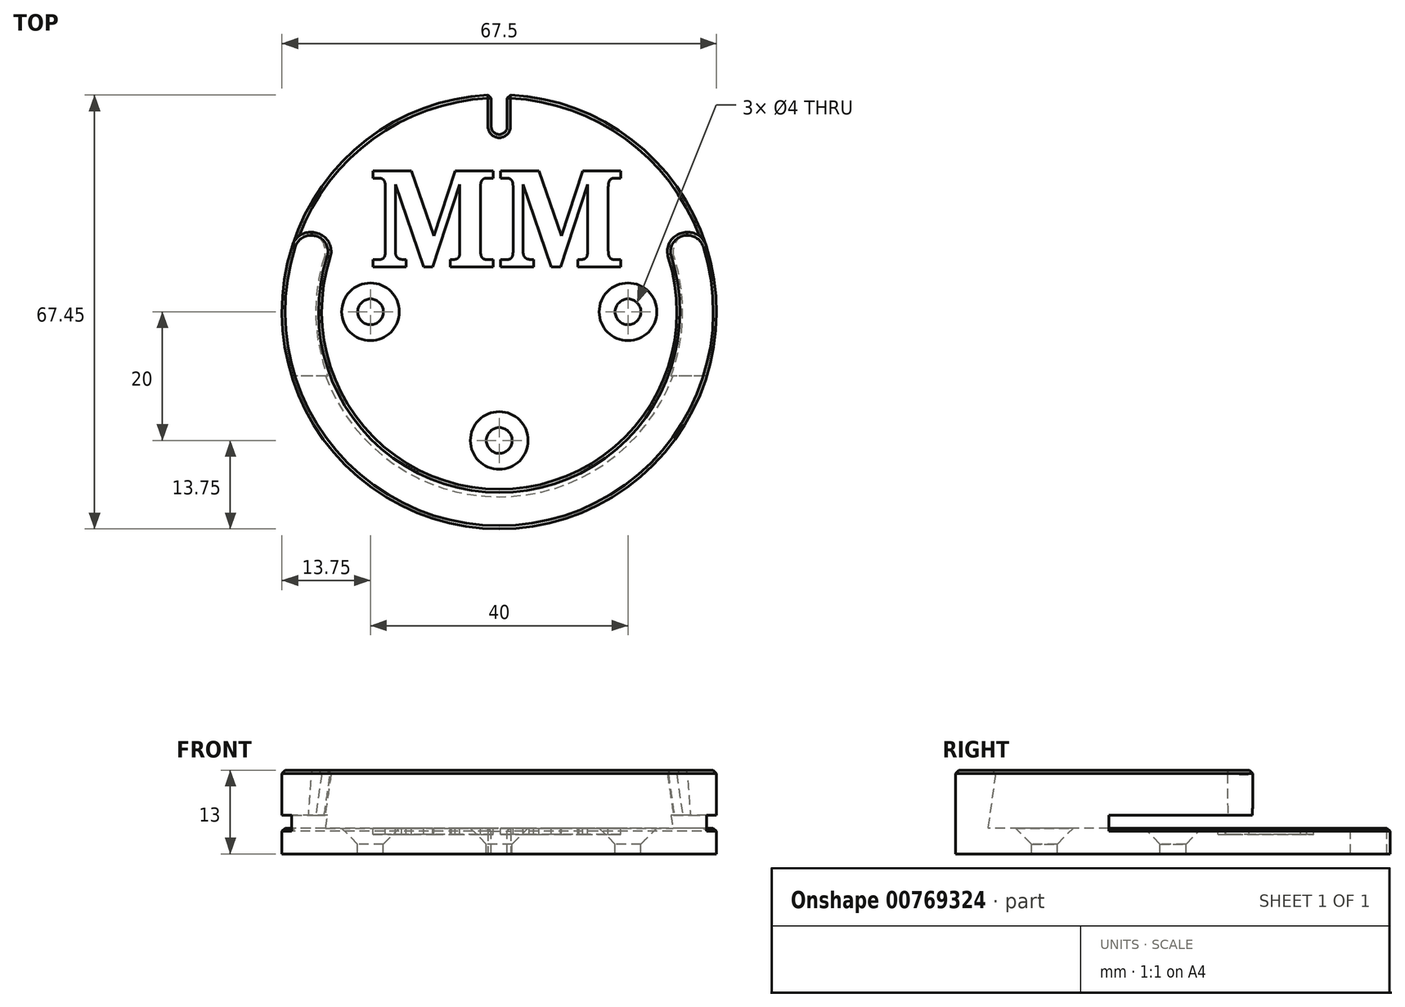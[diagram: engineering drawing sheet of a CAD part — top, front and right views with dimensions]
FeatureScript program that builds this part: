
annotation { "Feature Type Name" : "Feature", "Feature Type Description" : "" }
export const myFeature = defineFeature(function(context is Context, id is Id, definition is map)
    precondition{}
    {
        {
            var Q0;
            Q0=qCreatedBy(makeId("Top.planeOp"),FACE);
            var sketch = newSketch(context, id + "F0", { "sketchPlane" : qUnion([Q0])});
            skCircle(sketch, "E0", {"center": v(0, 0) * mm, "radius": 33.75 * mm});
            skSolve(sketch);
        }
        {
            var Q0;
            Q0 = qSketchRegion(id + "F0", true);
            extrude(context, id + "F1", {"entities" : qUnion([Q0]), "depth" : 13 * mm, "offsetDistance" : 25 * mm});
        }
        {
            var Q0;
            Q0=makeQuery(id+"F1.opExtrude","CAP_FACE",FACE,{"disambiguationData":[OSD([sQuery(id+"F0.wireOp",EDGE,"E0")])],"isStart":false});
            var sketch = newSketch(context, id + "F2", { "sketchPlane" : qUnion([Q0])});
            skCircle(sketch, "E1", {"center": v(0, 0) * mm, "radius": 27.5 * mm});
            skSolve(sketch);
        }
        {
            var Q0;
            Q0 = qSketchRegion(id + "F2", true);
            extrude(context, id + "F3", {"entities" : qUnion([Q0]), "operationType" : NewBodyOperationType.REMOVE, "oppositeDirection" : true, "depth" : 9 * mm, "offsetDistance" : 25 * mm, "hasDraft" : true, "draftAngle" : 8 * degree});
        }
        {
            var Q0;
            Q0=makeQuery(id+"F1.opExtrude","CAP_FACE",FACE,{"disambiguationData":[OSD([sQuery(id+"F0.wireOp",EDGE,"E0")])],"isStart":false});
            var sketch = newSketch(context, id + "F4", { "sketchPlane" : qUnion([Q0])});
            skLineSegment(sketch, "E2.bottom", {"start": v(-40, 56.82) * mm, "end": v(40, 56.82) * mm});
            skLineSegment(sketch, "E2.left", {"start": v(-40, 56.82) * mm, "end": v(-40, 12.37) * mm});
            skLineSegment(sketch, "E3", {"start": v(-40, 12.37) * mm, "end": v(40, 12.37) * mm});
            skLineSegment(sketch, "E4", {"start": v(40, 56.82) * mm, "end": v(40, 12.37) * mm});
            skSolve(sketch);
        }
        {
            var Q0;
            Q0 = qSketchRegion(id + "F4", true);
            extrude(context, id + "F5", {"entities" : qUnion([Q0]), "operationType" : NewBodyOperationType.REMOVE, "oppositeDirection" : true, "depth" : 9 * mm, "offsetDistance" : 25 * mm});
        }
        {
            var Q0;
            Q0=qCreatedBy(makeId("Front.planeOp"),FACE);
            var sketch = newSketch(context, id + "F6", { "sketchPlane" : qUnion([Q0])});
            skLineSegment(sketch, "E5.bottom", {"start": v(57, 6) * mm, "end": v(-73, 6) * mm});
            skLineSegment(sketch, "E5.top", {"start": v(57, 4) * mm, "end": v(-73, 4) * mm});
            skLineSegment(sketch, "E5.left", {"start": v(57, 6) * mm, "end": v(57, 4) * mm});
            skLineSegment(sketch, "E5.right", {"start": v(-73, 6) * mm, "end": v(-73, 4) * mm});
            skSolve(sketch);
        }
        {
            var Q0;
            Q0 = qSketchRegion(id + "F6", true);
            extrude(context, id + "F7", {"entities" : qUnion([Q0]), "operationType" : NewBodyOperationType.REMOVE, "depth" : 10 * mm, "offsetDistance" : 25 * mm, "hasSecondDirection" : true, "secondDirectionOppositeDirection" : true, "secondDirectionDepth" : 48.7 * mm});
        }
        {
            var Q0;
            Q0=makeQuery(id+"F7.boolean.opBoolean","MERGE",FACE,{"derivedFrom":[makeQuery(id+"F5.boolean.opBoolean","MERGE",FACE,{"derivedFrom":[makeQuery(id+"F3.boolean.opBoolean","COPY",FACE,{"derivedFrom":makeQuery(id+"F3.opExtrude","CAP_FACE",FACE,{"disambiguationData":[OSD([sQuery(id+"F2.wireOp",EDGE,"E1")])],"isStart":false})}),makeQuery(id+"F5.opExtrude","CAP_FACE",FACE,{"disambiguationData":[OSD([sQuery(id+"F4.wireOp",EDGE,"E2.bottom"),sQuery(id+"F4.wireOp",EDGE,"E2.top"),sQuery(id+"F4.wireOp",EDGE,"E2.left"),sQuery(id+"F4.wireOp",EDGE,"E2.right")])],"isStart":false})]}),makeQuery(id+"F7.opExtrude","SWEPT_FACE",FACE,{"disambiguationData":[OSD([sQuery(id+"F6.wireOp",EDGE,"E5.top")])]})]});
            var sketch = newSketch(context, id + "F8", { "sketchPlane" : qUnion([Q0])});
            skText(sketch, "E6", { "text": "MM", "fontName": "NotoSerif-Bold.ttf"});
            const initialGuessF8  = {"E6": [-0.02022, 0.007, 1, 0, 0.015]};
            skSetInitialGuess(sketch, initialGuessF8);
            skSolve(sketch);
        }
        {
            var Q0;
            Q0 = qSketchRegion(id + "F8", true);
            extrude(context, id + "F9", {"entities" : qUnion([Q0]), "operationType" : NewBodyOperationType.REMOVE, "oppositeDirection" : true, "depth" : 1 * mm, "offsetDistance" : 25 * mm});
        }
        {
            var Q0;
            Q0=makeQuery(id+"F5.boolean.opBoolean","INTERSECT",EDGE,{"disambiguationData":[OD(0.0)],"derivedFrom":[makeQuery(id+"F3.boolean.opBoolean","COPY",FACE,{"derivedFrom":makeQuery(id+"F3.opExtrude","SWEPT_FACE",FACE,{"disambiguationData":[OSD([sQuery(id+"F2.wireOp",EDGE,"E1")])]})}),makeQuery(id+"F5.opExtrude","SWEPT_FACE",FACE,{"disambiguationData":[OSD([sQuery(id+"F4.wireOp",EDGE,"E3")])]})]});
            var Q1;
            Q1=makeQuery(id+"F5.boolean.opBoolean","INTERSECT",EDGE,{"disambiguationData":[OD(0.0)],"derivedFrom":[makeQuery(id+"F1.opExtrude","SWEPT_FACE",FACE,{"disambiguationData":[OSD([sQuery(id+"F0.wireOp",EDGE,"E0")])]}),makeQuery(id+"F5.opExtrude","SWEPT_FACE",FACE,{"disambiguationData":[OSD([sQuery(id+"F4.wireOp",EDGE,"E3")])]})]});
            var Q2;
            Q2=makeQuery(id+"F5.boolean.opBoolean","INTERSECT",EDGE,{"disambiguationData":[OD(1.0)],"derivedFrom":[makeQuery(id+"F1.opExtrude","SWEPT_FACE",FACE,{"disambiguationData":[OSD([sQuery(id+"F0.wireOp",EDGE,"E0")])]}),makeQuery(id+"F5.opExtrude","SWEPT_FACE",FACE,{"disambiguationData":[OSD([sQuery(id+"F4.wireOp",EDGE,"E3")])]})]});
            var Q3;
            Q3=makeQuery(id+"F5.boolean.opBoolean","INTERSECT",EDGE,{"disambiguationData":[OD(1.0)],"derivedFrom":[makeQuery(id+"F3.boolean.opBoolean","COPY",FACE,{"derivedFrom":makeQuery(id+"F3.opExtrude","SWEPT_FACE",FACE,{"disambiguationData":[OSD([sQuery(id+"F2.wireOp",EDGE,"E1")])]})}),makeQuery(id+"F5.opExtrude","SWEPT_FACE",FACE,{"disambiguationData":[OSD([sQuery(id+"F4.wireOp",EDGE,"E3")])]})]});
            fillet(context, id + "F10", {"entities" : qUnion([Q0, Q1, Q2, Q3]), "radius" : 3 * mm, "tangentPropagation" : true, "allowEdgeOverflow" : false});
        }
        {
            var Q0;
            Q0=makeQuery(id+"F1.opExtrude","CAP_EDGE",EDGE,{"disambiguationData":[OSD([sQuery(id+"F0.wireOp",EDGE,"E0")])],"isStart":false});
            chamfer(context, id + "F11", {"entities" : qUnion([Q0]), "width" : 0.5 * mm, "tangentPropagation" : true});
        }
        {
            var Q0;
            Q0=makeQuery(id+"F7.boolean.opBoolean","MERGE",FACE,{"derivedFrom":[makeQuery(id+"F5.boolean.opBoolean","MERGE",FACE,{"derivedFrom":[makeQuery(id+"F3.boolean.opBoolean","COPY",FACE,{"derivedFrom":makeQuery(id+"F3.opExtrude","CAP_FACE",FACE,{"disambiguationData":[OSD([sQuery(id+"F2.wireOp",EDGE,"E1")])],"isStart":false})}),makeQuery(id+"F5.opExtrude","CAP_FACE",FACE,{"disambiguationData":[OSD([sQuery(id+"F4.wireOp",EDGE,"E2.bottom"),sQuery(id+"F4.wireOp",EDGE,"E2.left"),sQuery(id+"F4.wireOp",EDGE,"E3"),sQuery(id+"F4.wireOp",EDGE,"E4")])],"isStart":false})]}),makeQuery(id+"F7.opExtrude","SWEPT_FACE",FACE,{"disambiguationData":[OSD([sQuery(id+"F6.wireOp",EDGE,"E5.top")])]})]});
            var sketch = newSketch(context, id + "F12", { "sketchPlane" : qUnion([Q0])});
            skPoint(sketch, "E7", {"position": v(20, 0) * mm});
            skPoint(sketch, "E8", {"position": v(0, -20) * mm});
            skPoint(sketch, "E9", {"position": v(-20, 0) * mm});
            skSolve(sketch);
        }
        {
            var Q0;
            Q0=sQuery(id+"F12.wireOp",VERTEX,"E8");
            var Q1;
            Q1=sQuery(id+"F12.wireOp",VERTEX,"E7");
            var Q2;
            Q2=sQuery(id+"F12.wireOp",VERTEX,"E9");
            var Q3;
            Q3=makeQuery(id+"F1.opExtrude","SWEPT_BODY",BODY,{"disambiguationData":[OSD([sQuery(id+"F0.wireOp",EDGE,"E0")])]});
            hole(context, id + "F13", {"style" : HoleStyle.C_SINK, "endStyle" : HoleEndStyle.THROUGH, "holeDiameter" : 4 * mm, "cSinkDiameter" : 8.96 * mm, "cSinkAngle" : 90 * degree, "majorDiameter" : 5 * mm, "isTappedThrough" : true, "tappedDepth" : 12 * mm, "tapClearance" : 3, "startFromSketch" : true, "locations" : qUnion([Q0, Q1, Q2]), "scope" : qUnion([Q3])});
        }
        {
            var Q0;
            Q0=makeQuery(id+"F2.imprint","IMPRINT",FACE,{"disambiguationData":[TD([[makeQuery(id+"F2.imprint","IMPRINT",EDGE,{"derivedFrom":sQuery(id+"F2.wireOp",EDGE,"E1")}),-1.0]])]});
            var sketch = newSketch(context, id + "F14", { "sketchPlane" : qUnion([Q0])});
            skLineSegment(sketch, "E10.bottom", {"start": v(-1.25, 36.81) * mm, "end": v(1.25, 36.81) * mm});
            skLineSegment(sketch, "E10.left", {"start": v(-1.25, 36.81) * mm, "end": v(-1.25, 28.81) * mm});
            skLineSegment(sketch, "E10.right", {"start": v(1.25, 36.81) * mm, "end": v(1.25, 28.81) * mm});
            skArc(sketch, "E11", {"start": v(-1.25, 28.81) * mm, "mid": v(0, 27.56) * mm, "end": v(1.25, 28.81) * mm});
            skSolve(sketch);
        }
        {
            var Q0;
            Q0 = qSketchRegion(id + "F14", true);
            extrude(context, id + "F15", {"entities" : qUnion([Q0]), "operationType" : NewBodyOperationType.REMOVE, "oppositeDirection" : true, "depth" : 25 * mm, "offsetDistance" : 25 * mm});
        }
        {
            var Q0;
            {var subQ0=sQuery(id+"F6.wireOp",EDGE,"E5.top");var subQ1=makeQuery(id+"F7.opExtrude","SWEPT_FACE",FACE,{"disambiguationData":[OSD([subQ0])]});var subQ2=makeQuery(id+"F1.opExtrude","SWEPT_FACE",FACE,{"disambiguationData":[OSD([sQuery(id+"F0.wireOp",EDGE,"E0")])]});Q0=makeQuery(id+"F15.boolean.opBoolean","SPLIT",EDGE,{"disambiguationData":[TD([makeQuery(id+"F15.opExtrude","SWEPT_FACE",FACE,{"disambiguationData":[OSD([sQuery(id+"F14.wireOp",EDGE,"E10.right")])]})])],"derivedFrom":makeQuery(id+"F7.boolean.opBoolean","INTERSECT",EDGE,{"derivedFrom":[subQ2,subQ1]})});}
            var Q1;
            {var subQ0=sQuery(id+"F6.wireOp",EDGE,"E5.top");var subQ1=makeQuery(id+"F7.opExtrude","SWEPT_FACE",FACE,{"disambiguationData":[OSD([subQ0])]});var subQ2=makeQuery(id+"F1.opExtrude","SWEPT_FACE",FACE,{"disambiguationData":[OSD([sQuery(id+"F0.wireOp",EDGE,"E0")])]});Q1=makeQuery(id+"F15.boolean.opBoolean","SPLIT",EDGE,{"disambiguationData":[TD([makeQuery(id+"F15.opExtrude","SWEPT_FACE",FACE,{"disambiguationData":[OSD([sQuery(id+"F14.wireOp",EDGE,"E10.left")])]})])],"derivedFrom":makeQuery(id+"F7.boolean.opBoolean","INTERSECT",EDGE,{"derivedFrom":[subQ2,subQ1]})});}
            var Q2;
            Q2=makeQuery(id+"F15.boolean.opBoolean","INTERSECT",EDGE,{"derivedFrom":[makeQuery(id+"F7.boolean.opBoolean","MERGE",FACE,{"derivedFrom":[makeQuery(id+"F5.boolean.opBoolean","MERGE",FACE,{"derivedFrom":[makeQuery(id+"F3.boolean.opBoolean","COPY",FACE,{"derivedFrom":makeQuery(id+"F3.opExtrude","CAP_FACE",FACE,{"disambiguationData":[OSD([sQuery(id+"F2.wireOp",EDGE,"E1")])],"isStart":false})}),makeQuery(id+"F5.opExtrude","CAP_FACE",FACE,{"disambiguationData":[OSD([sQuery(id+"F4.wireOp",EDGE,"E2.bottom"),sQuery(id+"F4.wireOp",EDGE,"E2.left"),sQuery(id+"F4.wireOp",EDGE,"E3"),sQuery(id+"F4.wireOp",EDGE,"E4")])],"isStart":false})]}),makeQuery(id+"F7.opExtrude","SWEPT_FACE",FACE,{"disambiguationData":[OSD([sQuery(id+"F6.wireOp",EDGE,"E5.top")])]})]}),makeQuery(id+"F15.opExtrude","SWEPT_FACE",FACE,{"disambiguationData":[OSD([sQuery(id+"F14.wireOp",EDGE,"E10.right")])]})]});
            var Q3;
            Q3=makeQuery(id+"F15.boolean.opBoolean","INTERSECT",EDGE,{"derivedFrom":[makeQuery(id+"F1.opExtrude","SWEPT_FACE",FACE,{"disambiguationData":[OSD([sQuery(id+"F0.wireOp",EDGE,"E0")])]}),makeQuery(id+"F15.opExtrude","SWEPT_FACE",FACE,{"disambiguationData":[OSD([sQuery(id+"F14.wireOp",EDGE,"E10.right")])]})]});
            var Q4;
            Q4=makeQuery(id+"F15.boolean.opBoolean","INTERSECT",EDGE,{"derivedFrom":[makeQuery(id+"F1.opExtrude","SWEPT_FACE",FACE,{"disambiguationData":[OSD([sQuery(id+"F0.wireOp",EDGE,"E0")])]}),makeQuery(id+"F15.opExtrude","SWEPT_FACE",FACE,{"disambiguationData":[OSD([sQuery(id+"F14.wireOp",EDGE,"E10.left")])]})]});
            chamfer(context, id + "F16", {"entities" : qUnion([Q0, Q1, Q2, Q3, Q4]), "width" : 0.5 * mm, "tangentPropagation" : true});
        }
    });
